# Revit family: Shower-Shower_Trim-KOHLER-Purist-K-TS14422_1
name_source: partatom
category: Plumbing Fixtures
revit_build: Autodesk Revit 2015 (Build: 20140606_1530(x64)
units: mm (PartAtom-declared; Revit-internal decimal feet)

## types (1)
- Not a Type-See Type Catalog
    ADA Compliant = No
    Assembly Code = D2010700
    CW Connection = No
    Cold Water Inlet = Cold Water Inlet
    Cross Handle = Yes
    Date Modified = 05/16/2019
    Default Elevation = 42"
    Description = Rite-Temp(r) shower trim set with cross handle, valve not included
    Dist 1 = 1 3/4"
    Drain Included = No
    Finish = Default
    Flow Rate = 3 GPM
    HW Connection = Yes
    Handle Clearance = 3 1/2"
    Height = 6 1/2"
    Hot Water Inlet = Tempered Water Inlet
    Length = 10 5/8"
    Lever Handle = No
    Manufacturer = KOHLER Co.
    MasterFormat 1995 = 15410
    MasterFormat 2004 = 22.41.23
    Material = Premium Metal Construction
    Model = K-TS14422-3-CP
    Panel Thickness = 0"
    Pressure = 80.00 psi
    Product Documentation Link = https://www.us.kohler.com
    Product Name = Purist
    Product Page URL = http://www.us.kohler.com
    Type = 1
    URL = https://www.us.kohler.com
    Vent Connection = No
    Waste Connection = No
    Waste Water Outlet = Waste Water Outlet
    WaterSense Certified = No
    Width = 6 1/2"

## geometry (parser evidence)
native form markers: Sweep x9
no freeform markers — native parametric forms only
